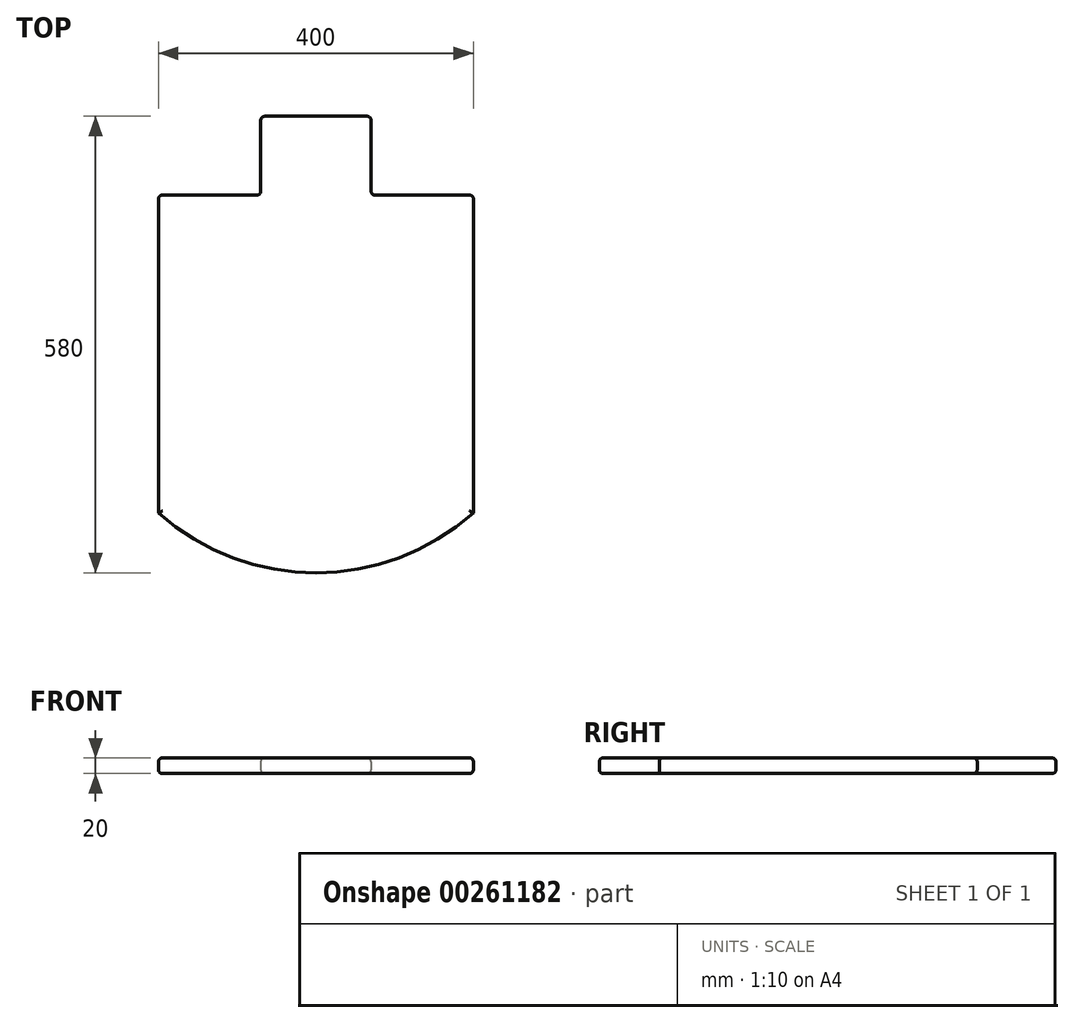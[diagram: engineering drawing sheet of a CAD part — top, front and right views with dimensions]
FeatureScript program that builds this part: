
annotation { "Feature Type Name" : "Feature", "Feature Type Description" : "" }
export const myFeature = defineFeature(function(context is Context, id is Id, definition is map)
    precondition{}
    {
        {
            var Q0;
            Q0=qCreatedBy(makeId("Top.planeOp"),FACE);
            var sketch = newSketch(context, id + "F0", { "sketchPlane" : qUnion([Q0])});
            skLineSegment(sketch, "E0", {"start": v(-70, 0) * mm, "end": v(70, 0) * mm});
            skLineSegment(sketch, "E1", {"start": v(70, 0) * mm, "end": v(70, -100) * mm});
            skLineSegment(sketch, "E2", {"start": v(70, -100) * mm, "end": v(200, -100) * mm});
            skLineSegment(sketch, "E3", {"start": v(200, -100) * mm, "end": v(200, -600) * mm});
            skLineSegment(sketch, "E4", {"start": v(200, -600) * mm, "end": v(-200, -600) * mm});
            skLineSegment(sketch, "E5", {"start": v(-200, -600) * mm, "end": v(-200, -100) * mm});
            skLineSegment(sketch, "E6", {"start": v(-200, -100) * mm, "end": v(-70, -100) * mm});
            skLineSegment(sketch, "E7", {"start": v(-70, -100) * mm, "end": v(-70, 0) * mm});
            skPoint(sketch, "E8", {"position": v(0, 0) * mm});
            skSolve(sketch);
        }
        {
            var Q0;
            Q0 = qSketchRegion(id + "F0", true);
            extrude(context, id + "F1", {"entities" : qUnion([Q0]), "depth" : 20 * mm});
        }
        {
            var Q0;
            Q0=makeQuery(id+"F1.opExtrude","CAP_FACE",FACE,{"disambiguationData":[OSD([sQuery(id+"F0.wireOp",EDGE,"E0"),sQuery(id+"F0.wireOp",EDGE,"E1"),sQuery(id+"F0.wireOp",EDGE,"E2"),sQuery(id+"F0.wireOp",EDGE,"E3"),sQuery(id+"F0.wireOp",EDGE,"E4"),sQuery(id+"F0.wireOp",EDGE,"E5"),sQuery(id+"F0.wireOp",EDGE,"E6"),sQuery(id+"F0.wireOp",EDGE,"E7")])],"isStart":false});
            var sketch = newSketch(context, id + "F2", { "sketchPlane" : qUnion([Q0])});
            skCircle(sketch, "E9", {"center": v(0, -280) * mm, "radius": 300 * mm});
            skSolve(sketch);
        }
        {
            var Q0;
            Q0 = qSketchRegion(id + "F2", true);
            extrude(context, id + "F3", {"entities" : qUnion([Q0]), "operationType" : NewBodyOperationType.INTERSECT, "endBound" : BoundingType.THROUGH_ALL, "oppositeDirection" : true, "depth" : 25 * mm});
        }
        {
            var Q0;
            Q0=makeQuery(id+"F3.boolean.opBoolean","COPY",FACE,{"derivedFrom":makeQuery(id+"F3.boolean.toolComplement.opBoolean","COPY",FACE,{"derivedFrom":makeQuery(id+"F3.opExtrude","SWEPT_FACE",FACE,{"disambiguationData":[OSD([sQuery(id+"F2.wireOp",EDGE,"E9")])]})})});
            var Q1;
            Q1=makeQuery(id+"F1.opExtrude","CAP_FACE",FACE,{"disambiguationData":[OSD([sQuery(id+"F0.wireOp",EDGE,"E0"),sQuery(id+"F0.wireOp",EDGE,"E1"),sQuery(id+"F0.wireOp",EDGE,"E2"),sQuery(id+"F0.wireOp",EDGE,"E3"),sQuery(id+"F0.wireOp",EDGE,"E4"),sQuery(id+"F0.wireOp",EDGE,"E5"),sQuery(id+"F0.wireOp",EDGE,"E6"),sQuery(id+"F0.wireOp",EDGE,"E7")])],"isStart":false});
            var Q2;
            Q2=makeQuery(id+"F1.opExtrude","SWEPT_FACE",FACE,{"disambiguationData":[OSD([sQuery(id+"F0.wireOp",EDGE,"E0")])]});
            var Q3;
            Q3=makeQuery(id+"F1.opExtrude","CAP_FACE",FACE,{"disambiguationData":[OSD([sQuery(id+"F0.wireOp",EDGE,"E0"),sQuery(id+"F0.wireOp",EDGE,"E1"),sQuery(id+"F0.wireOp",EDGE,"E2"),sQuery(id+"F0.wireOp",EDGE,"E3"),sQuery(id+"F0.wireOp",EDGE,"E4"),sQuery(id+"F0.wireOp",EDGE,"E5"),sQuery(id+"F0.wireOp",EDGE,"E6"),sQuery(id+"F0.wireOp",EDGE,"E7")])],"isStart":true});
            var Q4;
            Q4=makeQuery(id+"F1.opExtrude","SWEPT_FACE",FACE,{"disambiguationData":[OSD([sQuery(id+"F0.wireOp",EDGE,"E2")])]});
            var Q5;
            Q5=makeQuery(id+"F1.opExtrude","SWEPT_FACE",FACE,{"disambiguationData":[OSD([sQuery(id+"F0.wireOp",EDGE,"E6")])]});
            fillet(context, id + "F4", {"entities" : qUnion([Q0, Q1, Q2, Q3, Q4, Q5]), "radius" : 5 * mm, "tangentPropagation" : true, "allowEdgeOverflow" : false});
        }
    });
